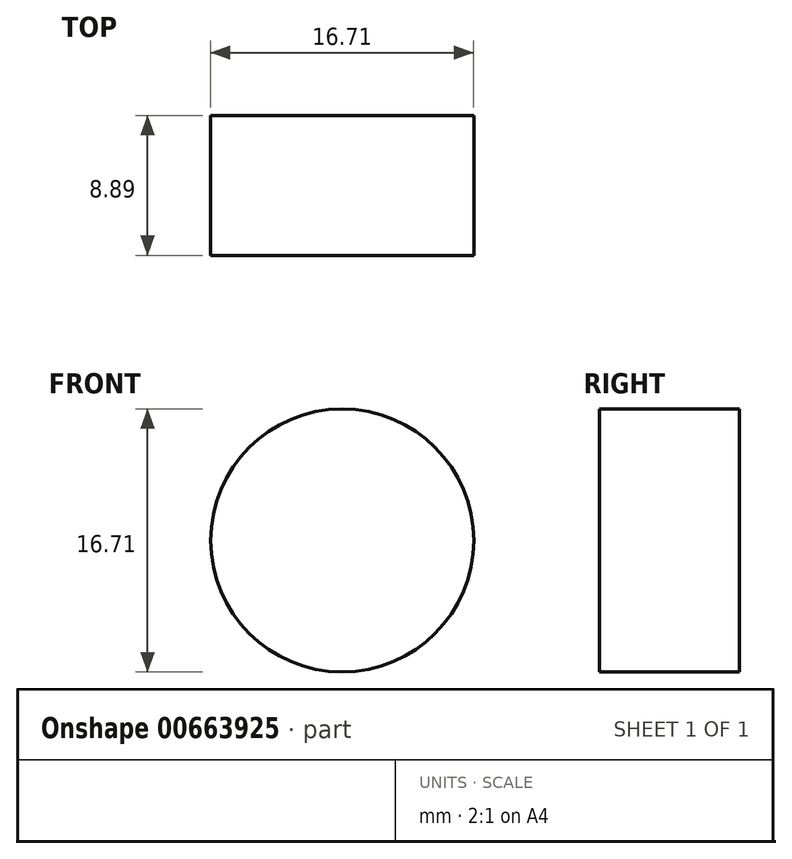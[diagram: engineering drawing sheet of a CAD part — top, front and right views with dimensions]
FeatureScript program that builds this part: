
annotation { "Feature Type Name" : "Feature", "Feature Type Description" : "" }
export const myFeature = defineFeature(function(context is Context, id is Id, definition is map)
    precondition{}
    {
        {
            var Q0;
            Q0=qCreatedBy(makeId("Front.planeOp"),FACE);
            var sketch = newSketch(context, id + "F0", { "sketchPlane" : qUnion([Q0])});
            skCircle(sketch, "E0", {"center": v(-135, 48.8) * mm, "radius": 8.36 * mm});
            skSolve(sketch);
        }
        {
            var Q0;
            Q0 = qSketchRegion(id + "F0", true);
            extrude(context, id + "F1", {"entities" : qUnion([Q0]), "depth" : -8.9 * mm, "offsetDistance" : 25.4 * mm});
        }
    });
